# Revit family: Toilet-Floor_Mount-KOHLER-Reach_Up-K-31116K_1
name_source: partatom
category: Plumbing Fixtures
units: mm (PartAtom-declared; Revit-internal decimal feet)

## family parameters
Cut with Voids When Loaded = No
Host = Face
OmniClass Number = 23.31.19.00
OmniClass Title = Toilets
Part Type = Normal
Room Calculation Point = No
Round Connector Dimension = Use Diameter
Shared = No

## types (2) — shared parameters
ADA Compliant = No
Assembly Code = D2010100
Bowl Height = 15 3/8"
CW Connection = Yes
Cold Water Inlet = Cold Water Inlet
Date Modified = 02/16/2023
Default Elevation = 0"
Description = 2 Piece Toilet,2.6/4L, S-trap 305mm
Finish = Kohler-Vitreous_China-0-White
Flow Rate = 0 GPM
Flush Rate- GPF = 1.05 GPF
Flush Rate- LPF = 4 LPF
HW Connection = No
Height = 29 1/2"
Hot Water Inlet = Hot Water Inlet
Length = 26 13/16"
Manufacturer = Kohler Co.
Master Format 2014 = 22 42 13.13
Master Format 2014 Name = Residential Water Closets
Material = Vitreous China
Pressure = 0.00 psi
Product Documentation Link = https://resources.kohler.com
Product Name = Reach Up
Product Page URL = https://www.kohlerasiapacific.com
Rough-In = 12"
URL = https://www.kohlerasiapacific.com
Vent Connection = No
Waste Connection = Yes
Waste Water Outlet = Waste Water Outlet
WaterSense Certified = No
Width = 15 3/8"

## per-type parameters (varying)
| type | Model | Seat Included | Type |
| With Seat,0-White | K-31116K-0 | Yes | 1 |
| Without Seat,0-White | K-31116K-HC-0 | No | 2 |

## geometry (parser evidence)
native form markers: Sweep x5
no freeform markers — native parametric forms only
